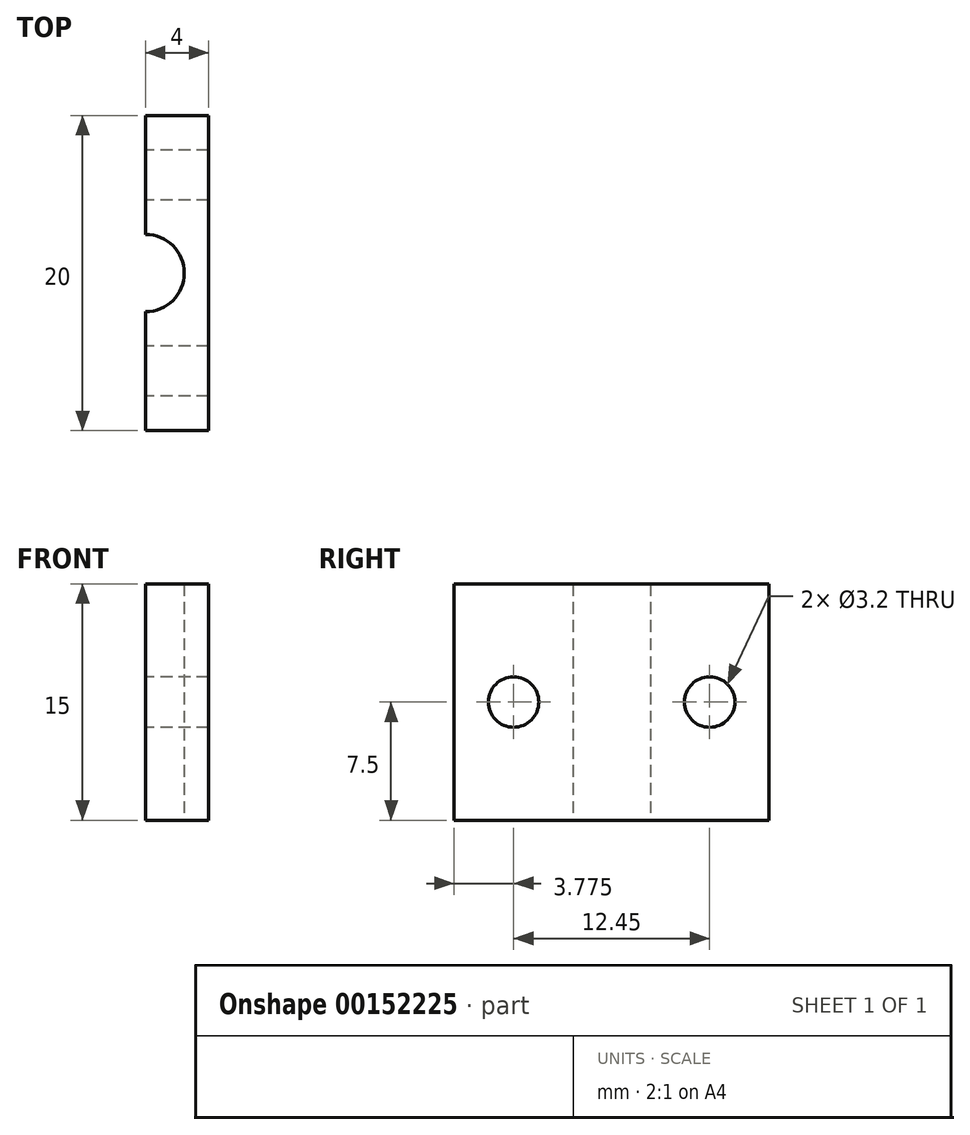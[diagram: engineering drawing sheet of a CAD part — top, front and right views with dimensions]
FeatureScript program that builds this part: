
annotation { "Feature Type Name" : "Feature", "Feature Type Description" : "" }
export const myFeature = defineFeature(function(context is Context, id is Id, definition is map)
    precondition{}
    {
        {
            var Q0;
            Q0=qCreatedBy(makeId("Top.planeOp"),FACE);
            var sketch = newSketch(context, id + "F0", { "sketchPlane" : qUnion([Q0])});
            skCircle(sketch, "E0", {"center": v(0, 0) * mm, "radius": 2.45 * mm});
            skCircle(sketch, "E1", {"center": v(0, 0) * mm, "radius": 4 * mm});
            skLineSegment(sketch, "E2.bottom", {"start": v(0, 0) * mm, "end": v(4, 0) * mm});
            skLineSegment(sketch, "E2.top", {"start": v(0, 10) * mm, "end": v(4, 10) * mm});
            skLineSegment(sketch, "E2.left", {"start": v(0, 0) * mm, "end": v(0, 10) * mm});
            skLineSegment(sketch, "E2.right", {"start": v(4, 0) * mm, "end": v(4, 10) * mm});
            skLineSegment(sketch, "E3.top", {"start": v(0, -10) * mm, "end": v(4, -10) * mm});
            skLineSegment(sketch, "E3.left", {"start": v(0, 0) * mm, "end": v(0, -10) * mm});
            skLineSegment(sketch, "E3.right", {"start": v(4, 0) * mm, "end": v(4, -10) * mm});
            skSolve(sketch);
        }
        {
            var Q0;
            {var subQ4=sQuery(id+"F0.wireOp",EDGE,"E2.top");Q0=makeQuery(id+"F0.imprint","IMPRINT",FACE,{"disambiguationData":[TD([[makeQuery(id+"F0.imprint","IMPRINT",EDGE,{"derivedFrom":subQ4}),-1.0]])]});}
            var Q1;
            {var subQ4=sQuery(id+"F0.wireOp",EDGE,"E3.top");Q1=makeQuery(id+"F0.imprint","IMPRINT",FACE,{"disambiguationData":[TD([[makeQuery(id+"F0.imprint","IMPRINT",EDGE,{"derivedFrom":subQ4}),1.0]])]});}
            var Q2;
            {var subQ0=sQuery(id+"F0.wireOp",EDGE,"E2.left");var subQ1=sQuery(id+"F0.wireOp",EDGE,"E0");var subQ2=makeQuery(id+"F0.imprint","INTERSECT",VERTEX,{"derivedFrom":[subQ1,subQ0]});Q2=makeQuery(id+"F0.imprint","IMPRINT",FACE,{"disambiguationData":[TD([[makeQuery(id+"F0.imprint","IMPRINT",EDGE,{"disambiguationData":[TD([[subQ2,1.0]])],"derivedFrom":subQ1}),-1.0]])]});}
            var Q3;
            {var subQ0=sQuery(id+"F0.wireOp",EDGE,"E2.bottom");var subQ1=sQuery(id+"F0.wireOp",EDGE,"E0");var subQ2=makeQuery(id+"F0.imprint","INTERSECT",VERTEX,{"derivedFrom":[subQ1,subQ0]});Q3=makeQuery(id+"F0.imprint","IMPRINT",FACE,{"disambiguationData":[TD([[makeQuery(id+"F0.imprint","IMPRINT",EDGE,{"disambiguationData":[TD([[subQ2,1.0]])],"derivedFrom":subQ1}),-1.0]])]});}
            extrude(context, id + "F1", {"entities" : qUnion([Q0, Q1, Q2, Q3]), "depth" : 15 * mm});
        }
        {
            var Q0;
            Q0=makeQuery(id+"F1.opExtrude","SWEPT_FACE",FACE,{"disambiguationData":[OSD([sQuery(id+"F0.wireOp",EDGE,"E3.left")])]});
            var sketch = newSketch(context, id + "F2", { "sketchPlane" : qUnion([Q0])});
            skLineSegment(sketch, "E4", {"start": v(10, 7.5) * mm, "end": v(2.45, 7.5) * mm});
            skCircle(sketch, "E5", {"center": v(6.23, 7.5) * mm, "radius": 1.6 * mm});
            skSolve(sketch);
        }
        {
            var Q0;
            Q0 = qSketchRegion(id + "F2", true);
            extrude(context, id + "F3", {"entities" : qUnion([Q0]), "operationType" : NewBodyOperationType.REMOVE, "oppositeDirection" : true, "depth" : 25 * mm});
        }
        {
            var Q0;
            Q0=makeQuery(id+"F1.opExtrude","SWEPT_FACE",FACE,{"disambiguationData":[OSD([sQuery(id+"F0.wireOp",EDGE,"E2.left")])]});
            var sketch = newSketch(context, id + "F4", { "sketchPlane" : qUnion([Q0])});
            skLineSegment(sketch, "E6", {"start": v(-2.45, 7.5) * mm, "end": v(-6.22, 7.5) * mm});
            skPoint(sketch, "E6.endSnap0", {"position": v(-6.22, 0) * mm});
            skCircle(sketch, "E7", {"center": v(-6.22, 7.5) * mm, "radius": 1.6 * mm});
            skSolve(sketch);
        }
        {
            var Q0;
            Q0 = qSketchRegion(id + "F4", true);
            extrude(context, id + "F5", {"entities" : qUnion([Q0]), "operationType" : NewBodyOperationType.REMOVE, "oppositeDirection" : true, "depth" : 25 * mm});
        }
    });
